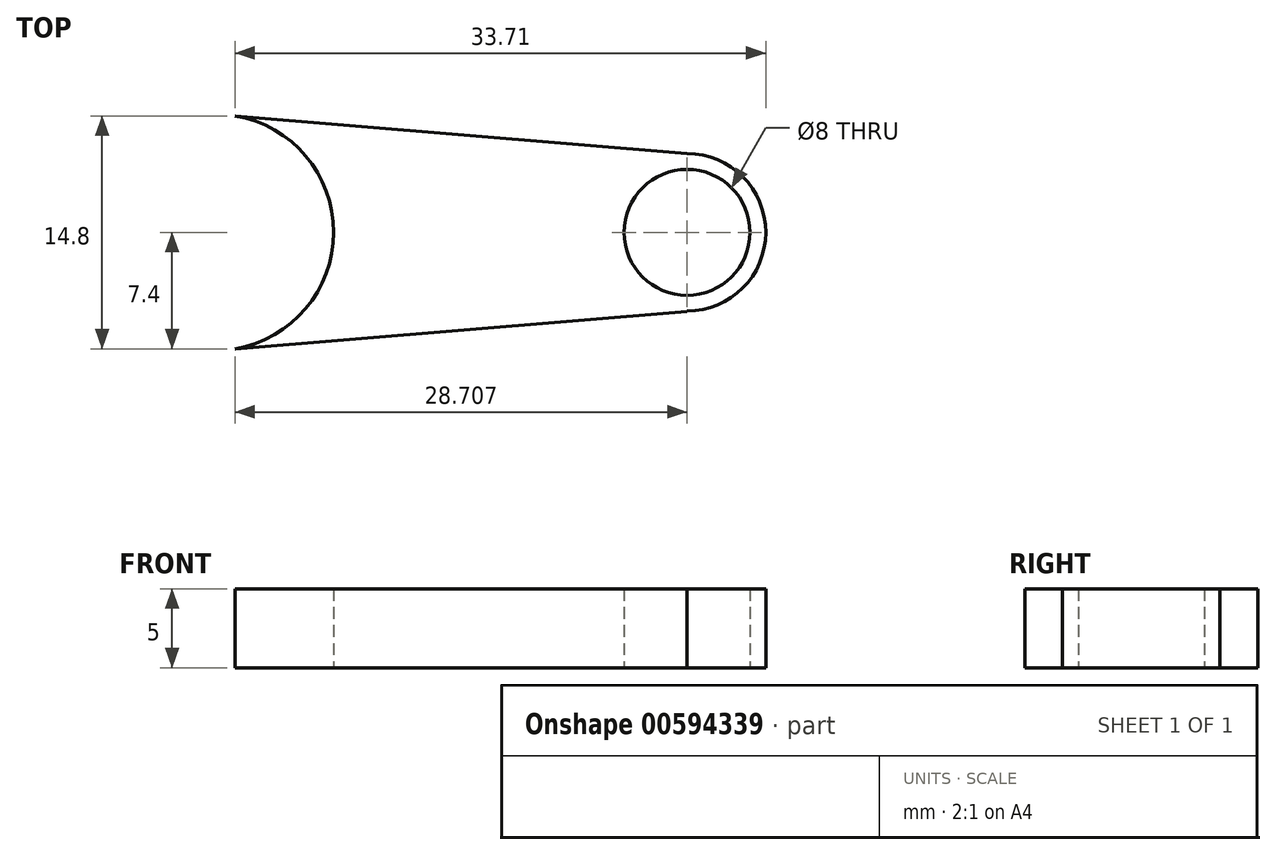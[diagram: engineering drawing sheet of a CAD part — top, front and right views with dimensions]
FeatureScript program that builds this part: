
annotation { "Feature Type Name" : "Feature", "Feature Type Description" : "" }
export const myFeature = defineFeature(function(context is Context, id is Id, definition is map)
    precondition{}
    {
        {
            var Q0;
            Q0=qCreatedBy(makeId("Top.planeOp"),FACE);
            var sketch = newSketch(context, id + "F0", { "sketchPlane" : qUnion([Q0])});
            skCircle(sketch, "E0", {"center": v(14.6, 0) * mm, "radius": 5 * mm});
            skCircle(sketch, "E1", {"center": v(-15.35, 0) * mm, "radius": 7.5 * mm});
            skLineSegment(sketch, "E2", {"start": v(-15.35, -7.5) * mm, "end": v(14.6, -5.02) * mm});
            skLineSegment(sketch, "E3", {"start": v(14.6, 5) * mm, "end": v(-15.35, 7.5) * mm});
            skLineSegment(sketch, "E4", {"start": v(14.6, 5) * mm, "end": v(14.6, 0) * mm});
            skLineSegment(sketch, "E5", {"start": v(14.6, -5.02) * mm, "end": v(14.6, 0) * mm});
            skSolve(sketch);
        }
        {
            var Q0;
            {var subQ0=sQuery(id+"F0.wireOp",EDGE,"E4");Q0=makeQuery(id+"F0.imprint","IMPRINT",FACE,{"disambiguationData":[TD([[makeQuery(id+"F0.imprint","IMPRINT",EDGE,{"derivedFrom":subQ0}),1.0]])]});}
            var Q1;
            {var subQ0=sQuery(id+"F0.wireOp",EDGE,"E4");Q1=makeQuery(id+"F0.imprint","IMPRINT",FACE,{"disambiguationData":[TD([[makeQuery(id+"F0.imprint","IMPRINT",EDGE,{"derivedFrom":subQ0}),-1.0]])]});}
            var Q2;
            {var subQ0=sQuery(id+"F0.wireOp",EDGE,"E3");var subQ3=sQuery(id+"F0.wireOp",EDGE,"E1");var subQ4=makeQuery(id+"F0.imprint","INTERSECT",VERTEX,{"disambiguationData":[OD(1.0)],"derivedFrom":[subQ3,subQ0]});Q2=makeQuery(id+"F0.imprint","IMPRINT",FACE,{"disambiguationData":[TD([[makeQuery(id+"F0.imprint","IMPRINT",EDGE,{"disambiguationData":[TD([[subQ4,1.0]])],"derivedFrom":subQ3}),-1.0]])]});}
            extrude(context, id + "F1", {"entities" : qUnion([Q0, Q1, Q2]), "depth" : 5 * mm, "offsetDistance" : 25.4 * mm});
        }
        {
            var Q0;
            Q0=makeQuery(id+"F1.opExtrude","CAP_FACE",FACE,{"disambiguationData":[OSD([sQuery(id+"F0.wireOp",EDGE,"E0"),sQuery(id+"F0.wireOp",EDGE,"E1"),sQuery(id+"F0.wireOp",EDGE,"E2"),sQuery(id+"F0.wireOp",EDGE,"E3"),sQuery(id+"F0.wireOp",EDGE,"E5")])],"isStart":true});
            var sketch = newSketch(context, id + "F2", { "sketchPlane" : qUnion([Q0])});
            skCircle(sketch, "E6", {"center": v(14.6, 0) * mm, "radius": 4 * mm});
            skSolve(sketch);
        }
        {
            var Q0;
            Q0=sQuery(id+"F2.wireOp",VERTEX,"E6.center");
            var Q1;
            Q1=makeQuery(id+"F1.opExtrude","SWEPT_BODY",BODY,{"disambiguationData":[OSD([sQuery(id+"F0.wireOp",EDGE,"E0"),sQuery(id+"F0.wireOp",EDGE,"E1"),sQuery(id+"F0.wireOp",EDGE,"E2"),sQuery(id+"F0.wireOp",EDGE,"E3"),sQuery(id+"F0.wireOp",EDGE,"E5")])]});
            hole(context, id + "F3", {"style" : HoleStyle.SIMPLE, "endStyle" : HoleEndStyle.THROUGH, "holeDiameter" : 8 * mm, "majorDiameter" : 6.35 * mm, "isTappedThrough" : true, "tappedDepth" : 12.7 * mm, "tapClearance" : 3, "locations" : qUnion([Q0]), "scope" : qUnion([Q1])});
        }
    });
